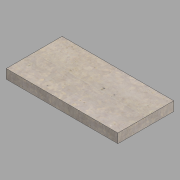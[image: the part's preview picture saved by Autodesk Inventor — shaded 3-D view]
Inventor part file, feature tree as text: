
AUTODESK INVENTOR PART (.ipt)
format: ipt  version: 2022 (Build 260153000, 153)  size: 118,272 bytes
history: native  units: in
note: dims shown in document units (in); Inventor stores cm internally (conversion verified against a paired STEP export)
features: other x1, extrude x1, sketch x1
ambient origin geometry x8: Origin, YZ Plane, XZ Plane, XY Plane, X Axis, Y Axis, Z Axis, Center Point
bodies: Body1 (feature_tree)
feature tree (3):
  other  "3x18x36 plinth paver"
  extrude  "Extrusion1"  Depth=18.0in
  sketch  "Sketch1"  dims[d0=36.0in d1=18.0in d2=3.0in d3=0.0in]
